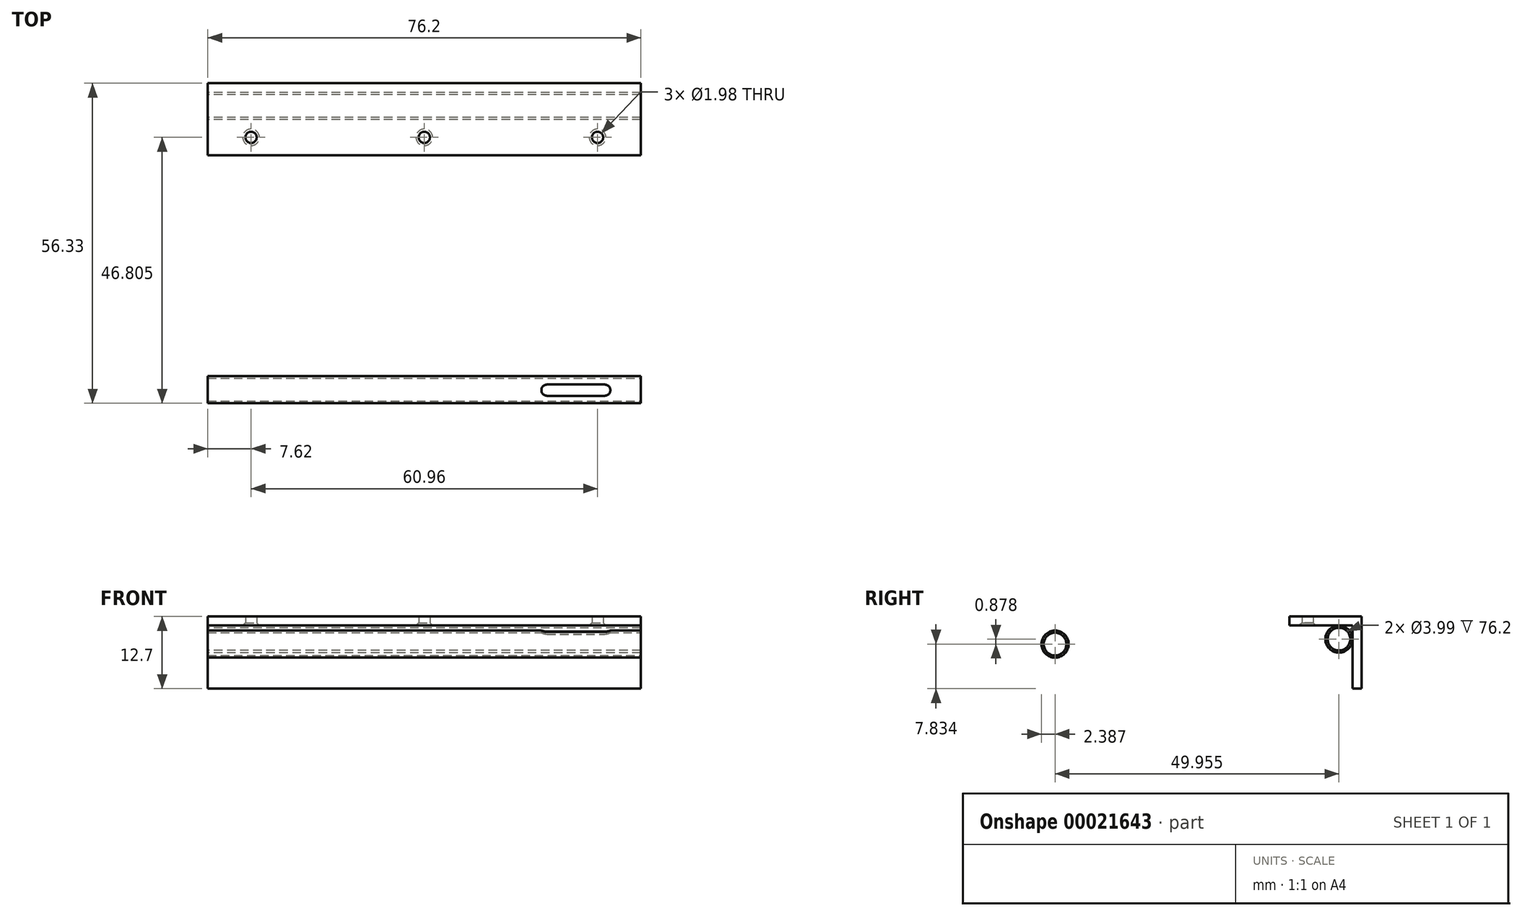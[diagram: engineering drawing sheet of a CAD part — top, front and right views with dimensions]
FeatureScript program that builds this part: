
annotation { "Feature Type Name" : "Feature", "Feature Type Description" : "" }
export const myFeature = defineFeature(function(context is Context, id is Id, definition is map)
    precondition{}
    {
        {
            var Q0;
            Q0=qCreatedBy(makeId("Right.planeOp"),FACE);
            var sketch = newSketch(context, id + "F0", { "sketchPlane" : qUnion([Q0])});
            skLineSegment(sketch, "E0", {"start": v(0, 0) * mm, "end": v(0, 12.7) * mm});
            skLineSegment(sketch, "E1", {"start": v(0, 12.7) * mm, "end": v(-12.7, 12.7) * mm});
            skLineSegment(sketch, "E2", {"start": v(-12.7, 12.7) * mm, "end": v(-12.7, 11.1) * mm});
            skLineSegment(sketch, "E3", {"start": v(-12.7, 11.1) * mm, "end": v(-1.6, 11.1) * mm});
            skLineSegment(sketch, "E4", {"start": v(-1.6, 11.1) * mm, "end": v(-1.6, 0) * mm});
            skLineSegment(sketch, "E5", {"start": v(-1.6, 0) * mm, "end": v(0, 0) * mm});
            skCircle(sketch, "E6", {"center": v(-3.99, 8.71) * mm, "radius": 2.39 * mm});
            skCircle(sketch, "E7", {"center": v(-3.99, 8.71) * mm, "radius": 2 * mm});
            skSolve(sketch);
        }
        {
            var Q0;
            Q0=makeQuery(id+"F0.imprint","IMPRINT",FACE,{"disambiguationData":[TD([[makeQuery(id+"F0.imprint","IMPRINT",EDGE,{"derivedFrom":sQuery(id+"F0.wireOp",EDGE,"E0")}),1.0]])]});
            var Q1;
            Q1=makeQuery(id+"F0.imprint","IMPRINT",FACE,{"disambiguationData":[TD([[makeQuery(id+"F0.imprint","IMPRINT",EDGE,{"derivedFrom":sQuery(id+"F0.wireOp",EDGE,"E7")}),-1.0]])]});
            extrude(context, id + "F1", {"entities" : qUnion([Q0, Q1]), "depth" : 76.2 * mm});
        }
        {
            var Q0;
            Q0=makeQuery(id+"F1.opExtrude","SWEPT_FACE",FACE,{"disambiguationData":[OSD([sQuery(id+"F0.wireOp",EDGE,"E3")])]});
            var sketch = newSketch(context, id + "F2", { "sketchPlane" : qUnion([Q0])});
            skLineSegment(sketch, "E8", {"start": v(38.1, 12.7) * mm, "end": v(38.1, 9.52) * mm});
            skSolve(sketch);
        }
        {
            var Q0;
            Q0=sQuery(id+"F2.wireOp",VERTEX,"E8.end");
            var Q1;
            Q1=makeQuery(id+"F1.opExtrude","SWEPT_BODY",BODY,{"disambiguationData":[OSD([sQuery(id+"F0.wireOp",EDGE,"E0"),sQuery(id+"F0.wireOp",EDGE,"E1"),sQuery(id+"F0.wireOp",EDGE,"E2"),sQuery(id+"F0.wireOp",EDGE,"E3"),sQuery(id+"F0.wireOp",EDGE,"E4"),sQuery(id+"F0.wireOp",EDGE,"E5")])]});
            hole(context, id + "F3", {"style" : HoleStyle.C_SINK, "holeDiameter" : 1.98 * mm, "cSinkDiameter" : 2.92 * mm, "endStyle" : HoleEndStyle.THROUGH, "locations" : qUnion([Q0]), "scope" : qUnion([Q1]), "cSinkAngle" : 90 * degree});
        }
        {
            var Q0;
            Q0=makeQuery(id+"F1.opExtrude","SWEPT_FACE",FACE,{"disambiguationData":[OSD([sQuery(id+"F0.wireOp",EDGE,"E3")])]});
            var sketch = newSketch(context, id + "F4", { "sketchPlane" : qUnion([Q0])});
            skLineSegment(sketch, "E9", {"start": v(38.1, 9.52) * mm, "end": v(7.62, 9.52) * mm});
            skLineSegment(sketch, "E10", {"start": v(38.1, 9.52) * mm, "end": v(68.58, 9.52) * mm});
            skSolve(sketch);
        }
        {
            var Q0;
            Q0=sQuery(id+"F4.wireOp",VERTEX,"E9.end");
            var Q1;
            Q1=sQuery(id+"F4.wireOp",VERTEX,"E10.end");
            var Q2;
            Q2=makeQuery(id+"F1.opExtrude","SWEPT_BODY",BODY,{"disambiguationData":[OSD([sQuery(id+"F0.wireOp",EDGE,"E0"),sQuery(id+"F0.wireOp",EDGE,"E1"),sQuery(id+"F0.wireOp",EDGE,"E2"),sQuery(id+"F0.wireOp",EDGE,"E3"),sQuery(id+"F0.wireOp",EDGE,"E4"),sQuery(id+"F0.wireOp",EDGE,"E5")])]});
            hole(context, id + "F5", {"style" : HoleStyle.C_SINK, "holeDiameter" : 1.98 * mm, "cSinkDiameter" : 2.92 * mm, "endStyle" : HoleEndStyle.THROUGH, "locations" : qUnion([Q0, Q1]), "scope" : qUnion([Q2]), "cSinkAngle" : 90 * degree});
        }
        {
            var Q0;
            Q0=qCreatedBy(makeId("Right.planeOp"),FACE);
            var sketch = newSketch(context, id + "F6", { "sketchPlane" : qUnion([Q0])});
            skLineSegment(sketch, "E11", {"start": v(-57.2, 11) * mm, "end": v(-57.2, 4.66) * mm});
            skLineSegment(sketch, "E12", {"start": v(-57.2, 4.66) * mm, "end": v(-50.85, 4.8) * mm});
            skLineSegment(sketch, "E13", {"start": v(-57.2, 11) * mm, "end": v(-50.85, 11) * mm});
            skLineSegment(sketch, "E14", {"start": v(-50.85, 11) * mm, "end": v(-50.85, 4.8) * mm});
            skLineSegment(sketch, "E15", {"start": v(-54.02, 11) * mm, "end": v(-54.02, 7.83) * mm});
            skSolve(sketch);
        }
        {
            var Q0;
            Q0 = qSketchRegion(id + "F6", true);
            extrude(context, id + "F7", {"entities" : qUnion([Q0]), "depth" : 76.2 * mm});
        }
        {
            var Q0;
            Q0=makeQuery(id+"F7.opExtrude","SWEPT_FACE",FACE,{"disambiguationData":[OSD([sQuery(id+"F6.wireOp",EDGE,"E13")])]});
            var sketch = newSketch(context, id + "F8", { "sketchPlane" : qUnion([Q0])});
            skLineSegment(sketch, "E16", {"start": v(69.85, -55.01) * mm, "end": v(59.7, -55.01) * mm});
            skLineSegment(sketch, "E17", {"start": v(59.7, -53.03) * mm, "end": v(69.85, -53.03) * mm});
            skArc(sketch, "E18", {"start": v(69.85, -55.01) * mm, "mid": v(70.84, -54.02) * mm, "end": v(69.85, -53.03) * mm});
            skArc(sketch, "E19", {"start": v(59.7, -53.03) * mm, "mid": v(58.7, -54.02) * mm, "end": v(59.7, -55.01) * mm});
            skSolve(sketch);
        }
        {
            var Q0;
            Q0 = qSketchRegion(id + "F8", true);
            extrude(context, id + "F9", {"entities" : qUnion([Q0]), "operationType" : NewBodyOperationType.REMOVE, "oppositeDirection" : true, "depth" : 3.17 * mm});
        }
        {
            var Q0;
            Q0=makeQuery(id+"F7.opExtrude","CAP_FACE",FACE,{"disambiguationData":[OSD([sQuery(id+"F6.wireOp",EDGE,"E11"),sQuery(id+"F6.wireOp",EDGE,"E12"),sQuery(id+"F6.wireOp",EDGE,"E13"),sQuery(id+"F6.wireOp",EDGE,"E14")])],"isStart":false});
            var sketch = newSketch(context, id + "F10", { "sketchPlane" : qUnion([Q0])});
            skLineSegment(sketch, "E20", {"start": v(-54.02, 11) * mm, "end": v(-54.02, 7.83) * mm});
            skCircle(sketch, "E21", {"center": v(-53.94, 7.83) * mm, "radius": 2.39 * mm});
            skCircle(sketch, "E22", {"center": v(-53.94, 7.83) * mm, "radius": 2 * mm});
            skSolve(sketch);
        }
        {
            var Q0;
            Q0 = qSketchRegion(id + "Fo5FQ4fOZP4kmmM_3", true);
            var Q1;
            Q1=makeQuery(id+"F10.imprint","IMPRINT",FACE,{"disambiguationData":[TD([[makeQuery(id+"F10.imprint","IMPRINT",EDGE,{"derivedFrom":sQuery(id+"F10.wireOp",EDGE,"E21")}),-1.0]])]});
            extrude(context, id + "F11", {"entities" : qUnion([Q0, Q1]), "operationType" : NewBodyOperationType.REMOVE, "oppositeDirection" : true, "depth" : 76.2 * mm});
        }
        {
            var Q0;
            Q0=makeQuery(id+"F7.opExtrude","CAP_FACE",FACE,{"disambiguationData":[OSD([sQuery(id+"F6.wireOp",EDGE,"E11"),sQuery(id+"F6.wireOp",EDGE,"E12"),sQuery(id+"F6.wireOp",EDGE,"E13"),sQuery(id+"F6.wireOp",EDGE,"E14")])],"isStart":false});
            var sketch = newSketch(context, id + "F12", { "sketchPlane" : qUnion([Q0])});
            skCircle(sketch, "E23", {"center": v(-53.94, 7.83) * mm, "radius": 2 * mm});
            skSolve(sketch);
        }
        {
            var Q0;
            Q0=makeQuery(id+"F12.imprint","IMPRINT",FACE,{"disambiguationData":[TD([[makeQuery(id+"F12.imprint","IMPRINT",EDGE,{"derivedFrom":sQuery(id+"F12.wireOp",EDGE,"E23")}),1.0]])]});
            extrude(context, id + "F13", {"entities" : qUnion([Q0]), "operationType" : NewBodyOperationType.REMOVE, "oppositeDirection" : true, "depth" : 76.2 * mm});
        }
    });
